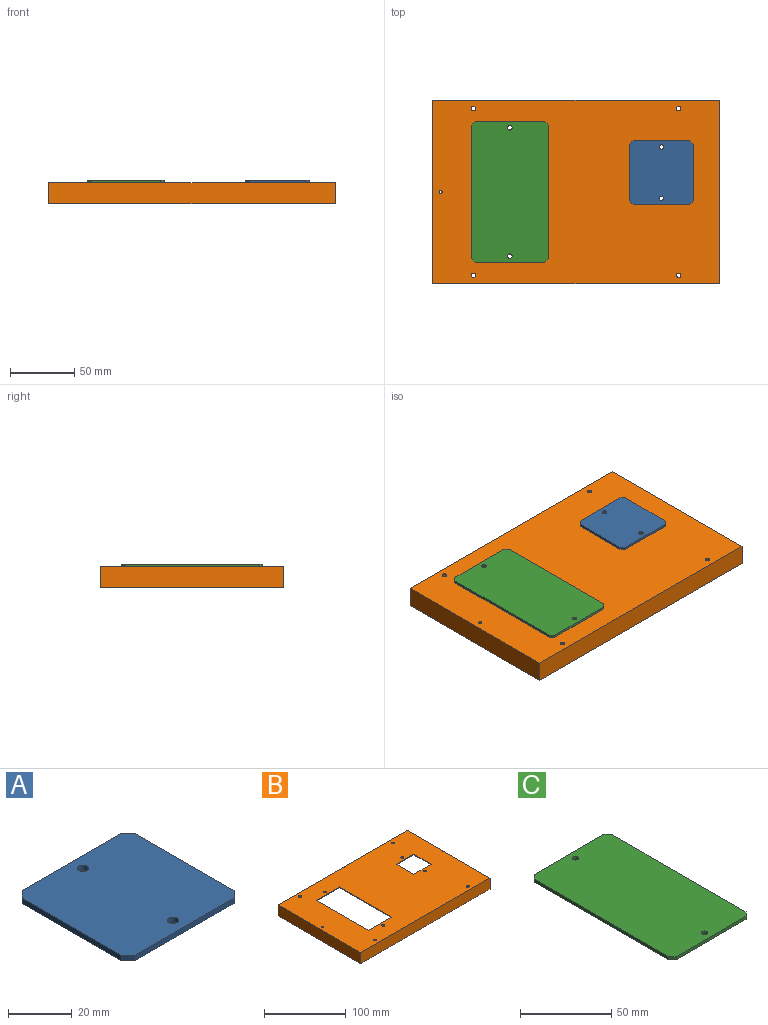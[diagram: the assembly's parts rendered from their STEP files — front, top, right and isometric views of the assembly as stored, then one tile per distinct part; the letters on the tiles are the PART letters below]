
ASSEMBLY  parts=3 mates=6
PART A: 12 faces, bbox 50x50x2 mm
  f0: plane 44x2mm, normal (0,1,0), area 88mm2, adj f4,f5,f8,f9
  f1: plane 44x2mm, normal (-1,0,0), area 88mm2, adj f4,f5,f8,f11
  f2: plane 44x2mm, normal (0,-1,0), area 88mm2, adj f4,f5,f10,f11
  f3: plane 44x2mm, normal (1,0,0), area 88mm2, adj f4,f5,f9,f10
  f4: plane 50x50mm, normal (0,0,1), area 2462.8mm2, adj f0,f1,f2,f3,f6,f7,f8,f9
  f5: plane 50x50mm, normal (0,0,-1), area 2462.8mm2, adj f0,f1,f2,f3,f6,f7,f8,f9
  f6: cylinder r=1.75mm len=3.5mm, axis (0,0,-1), area 22mm2, adj f4,f5
  f7: cylinder r=1.75mm len=3.5mm, axis (0,0,-1), area 22mm2, adj f4,f5
  f8: plane 3x3mm, normal (-0.71,0.71,0), area 8.5mm2, adj f0,f1,f4,f5
  f9: plane 3x3mm, normal (0.71,0.71,0), area 8.5mm2, adj f0,f3,f4,f5
  f10: plane 3x3mm, normal (0.71,-0.71,0), area 8.5mm2, adj f2,f3,f4,f5
  f11: plane 3x3mm, normal (-0.71,-0.71,0), area 8.5mm2, adj f1,f2,f4,f5
PART B: 28 faces, bbox 223x143x16.5 mm
  f0: plane 223x143mm, normal (0,0,-1), area 728mm2, adj f1,f2,f3,f4,f6,f7,f8,f9
  f1: plane 223x16.5mm, normal (0,1,0), area 3679.5mm2, adj f0,f2,f4,f5
  f2: plane 143x16.5mm, normal (-1,0,0), area 2359.5mm2, adj f0,f1,f3,f5
  f3: plane 223x16.5mm, normal (0,-1,0), area 3679.5mm2, adj f0,f2,f4,f5
  f4: plane 143x16.5mm, normal (1,0,0), area 2359.5mm2, adj f0,f1,f3,f5
  f5: plane 223x143mm, normal (0,0,1), area 27307.1mm2, adj f1,f2,f3,f4,f11,f12,f13,f14
  f6: plane 221x15.5mm, normal (0,-1,0), area 3425.5mm2, adj f0,f7,f9,f10
  f7: plane 141x15.5mm, normal (1,0,0), area 2185.5mm2, adj f0,f6,f8,f10
  f8: plane 221x15.5mm, normal (0,1,0), area 3425.5mm2, adj f0,f7,f9,f10
  f9: plane 141x15.5mm, normal (-1,0,0), area 2185.5mm2, adj f0,f6,f8,f10
  f10: plane 221x141mm, normal (0,0,-1), area 26579.1mm2, adj f6,f7,f8,f9,f11,f12,f13,f14
  f11: plane 30x1mm, normal (-1,0,0), area 30mm2, adj f5,f10,f12,f13
  f12: plane 30x1mm, normal (0,1,0), area 30mm2, adj f5,f10,f11,f14
  f13: plane 30x1mm, normal (0,-1,0), area 30mm2, adj f5,f10,f11,f14
  f14: plane 30x1mm, normal (1,0,0), area 30mm2, adj f5,f10,f12,f13
  f15: plane 90x1mm, normal (1,0,0), area 90mm2, adj f5,f10,f16,f17
  f16: plane 40x1mm, normal (0,-1,0), area 40mm2, adj f5,f10,f15,f18
  f17: plane 40x1mm, normal (0,1,0), area 40mm2, adj f5,f10,f15,f18
  f18: plane 90x1mm, normal (-1,0,0), area 90mm2, adj f5,f10,f16,f17
  f19: cylinder r=1.75mm len=3.5mm, axis (0,0,1), area 11mm2, adj f5,f10
  f20: cylinder r=1.75mm len=3.5mm, axis (0,0,1), area 11mm2, adj f5,f10
  f21: cylinder r=1.75mm len=3.5mm, axis (0,0,1), area 11mm2, adj f5,f10
  f22: cylinder r=1.75mm len=3.5mm, axis (0,0,1), area 11mm2, adj f5,f10
  f23: cylinder r=1.75mm len=3.5mm, axis (0,0,1), area 11mm2, adj f5,f10
  f24: cylinder r=1.75mm len=3.5mm, axis (0,0,1), area 11mm2, adj f5,f10
  f25: cylinder r=1.75mm len=3.5mm, axis (0,0,1), area 11mm2, adj f5,f10
  f26: cylinder r=1.75mm len=3.5mm, axis (0,0,1), area 11mm2, adj f5,f10
  f27: cylinder r=1.25mm len=2.5mm, axis (0,0,1), area 7.9mm2, adj f5,f10
PART C: 12 faces, bbox 60x110x2 mm
  f0: plane 54x2mm, normal (0,1,0), area 108mm2, adj f4,f5,f6,f7
  f1: plane 104x2mm, normal (-1,0,0), area 208mm2, adj f4,f5,f6,f9
  f2: plane 54x2mm, normal (0,-1,0), area 108mm2, adj f4,f5,f8,f9
  f3: plane 104x2mm, normal (1,0,0), area 208mm2, adj f4,f5,f7,f8
  f4: plane 110x60mm, normal (0,0,1), area 6562.8mm2, adj f0,f1,f2,f3,f6,f7,f8,f9
  f5: plane 110x60mm, normal (0,0,-1), area 6562.8mm2, adj f0,f1,f2,f3,f6,f7,f8,f9
  f6: plane 3x3mm, normal (-0.71,0.71,0), area 8.5mm2, adj f0,f1,f4,f5
  f7: plane 3x3mm, normal (0.71,0.71,0), area 8.5mm2, adj f0,f3,f4,f5
  f8: plane 3x3mm, normal (0.71,-0.71,0), area 8.5mm2, adj f2,f3,f4,f5
  f9: plane 3x3mm, normal (-0.71,-0.71,0), area 8.5mm2, adj f1,f2,f4,f5
  f10: cylinder r=1.75mm len=3.5mm, axis (0,0,1), area 22mm2, adj f4,f5
  f11: cylinder r=1.75mm len=3.5mm, axis (0,0,1), area 22mm2, adj f4,f5
PLACE A t=(157.85,59.48,67.45)mm
PLACE B t=(-20.15,115.98,67.45)mm
PLACE C t=(39.85,44.48,67.45)mm
MATE slider B.f22 <-> C.f10  axis (0,0,1) through (39.85,-5.52,67.45)mm
MATE planar C.f5 <-> B.f5  axis (0,0,-1) through (39.85,44.48,67.45)mm
MATE slider B.f20 <-> A.f7  axis (0,0,1) through (157.85,79.48,67.45)mm
MATE planar C.f5 <-> A.f5  axis (0,0,-1) through (39.85,44.48,67.45)mm
MATE slider B.f21 <-> A.f6  axis (0,0,1) through (157.85,39.48,67.45)mm
MATE slider B.f26 <-> C.f11  axis (0,0,1) through (39.85,94.48,67.45)mm
